# Revit family: Electrical_Switchgear_Modelec_Confidence-Collection-Single_FRA888
name_source: partatom
category: Installations électriques
units: mm (PartAtom-declared; Revit-internal decimal feet)

## family parameters
Conserver l'orientation des annotations = Non
Cote de connecteur circulaire = Utiliser le diamètre
Couper avec des vides une fois chargée = Non
Hôte = Face
Numéro OmniClass = 23.80.50.11.14
Partagée = Non
Repere pour localisation dans la piece = Non
Titre OmniClass = Switches
Type d'élément = Normal

## types (1)
- Par défaut - veuillez charger le catalogue des types de familles Revit
    Apparent Load = 0 VA
    B1 = Oui
    B1 + P1 = Non
    B2 = Non
    B3 = Non
    Bouton Bas = Non
    Bouton Droit = Non
    Bouton Gauche = Non
    Bouton Haut = Non
    Bouton de Masquage de la Zone Centrale Visible = Non
    C1 = Non
    C3 = Non
    Commutateur de Carte = Non
    Couleur du Mécanisme = Modelec - Metal - Noir Mat
    Description = Les interrupteurs de confiance et les plaques de couverture de prises en laiton, fabriqués en France, offrent un large éventail de fonctions : boutons poussoirs et bascules dans 4 finitions, avec ou sans LED, prises, prises Schuko, chargeurs USB, RJ45, HDMI, variateurs, volets roulants et bien plus encore. La collection Confiance est un grand classique du monde de la décoration. Ses formes épurées et le détail de ses finitions soignées en font un incontournable pour vos projets résidentiels, hôteliers ou tertiaires. La collection Confiance mérite son nom. La bonne touche, quel que soit votre choix esthétique. Disponible en 12 finitions.
    Description du Connecteur = Interrupteur
    Détecteur Mouv = Non
    Elévation par défaut = 0 mm  [stored 0 ft]
    Fabricant = Modelec
    Installation instructions = https://www.modelec.com
    K1 = Non
    LED Centre = Non
    LEDs sur les Côtés = Non
    Levier Centre = Oui
    Levier Droit = Non
    Levier Gauche = Non
    M1 = Non
    M2 = Non
    Modèle = Confidence Collection
    Number of Poles = 1
    P1 = Non
    P1 BL = Non
    P2 = Non
    P2 Vertical = Non
    P3 = Non
    P4 = Non
    Power Factor = 1
    Product Documentation Link = https://www.modelec.com
    Product Page URL = https://www.modelec.com
    Product data url = https://bimobject.com
    Quantité 1 = 3
    Quantité 2 = 3
    R1 = Non
    SC = Non
    U1 = Non
    URL = https://www.modelec.com
    V1 = Non
    Variateur Bluetooth = Non
    Version = 1
    Voltage = 220 V
    Weight - Mass = 0.12 kg

note: [stored X ft] marks values corroborated as IEEE doubles in the binary element streams (Revit-internal decimal feet)

## geometry (parser evidence)
native form markers: Sweep x2
no freeform markers — native parametric forms only
